# Revit family: Electronics_Touch-Panels_Biamp_Apprimo_Touch-7__
name_source: partatom
category: Communication Devices
units: mm (PartAtom-declared; Revit-internal decimal feet)

## family parameters
Cut with Voids When Loaded = No
Host = Face
Maintain Annotation Orientation = No
OmniClass Number = 23.85.10.17.11
OmniClass Title = Audio-Visual System Components
Part Type = Normal
Room Calculation Point = No
Round Connector Dimension = Use Diameter
Shared = No

## types (2) — shared parameters
Altitude = 0-6,600 ft (0-2000m) MSL
Apparent Load = 0 VA
Compliance = CE marked (Europe), RoHS Directive (Europe)
Connector Description = PoE (IEEE 802.3at Class 3,15W)
Controller Compatibility = Impera Alfa II, Impera Lima, Impera Tango, Impera Sierra II
Default Elevation = 48 "
Depth = 1.6 "
Description = Apprimo Touch 7 Touch Panel
Display Diagonal Size = 7 "
Display Resolution = 1024x595
Display Type = High-Contrast Capacitive Touch LCD
Height = 4.7 "
Humidity = 10-90% relative humidity (non-condensing)
Included Accessories = Mounting bracket  and screws, Ejector Pin, USB-OTG adapter, Polishing cloth
Manufacturer = Biamp
Max Power Consumption = 0 W
Maximum Display Brightness = 350 nits
Mini USB port = USB 2.0
Model = Apprimo Touch 7
Network Connection = RJ-45 with Ethernet cable (Cat 5e and above)
Number of Poles = 1
Power Factor = 1
Product Documentation Link = https://downloads.biamp.com
Product Page URL = https://www.biamp.com
Product data url = https://www.bimobject.com
Sensors = Proximity Ambient Light
Temperature Range = 32 - 104° F (0 - 40° C)
URL = https://www.biamp.com
Voltage = 0 V
Weight = 0.73 lbf
Width = 7 "

## per-type parameters (varying)
| type | Housing Material |
| Touch 7 White | Biamp - Plastic - White |
| Touch 7 Black | Biamp - Plastic - Black |

## geometry (parser evidence)
native form markers: Sweep x5
no freeform markers — native parametric forms only
